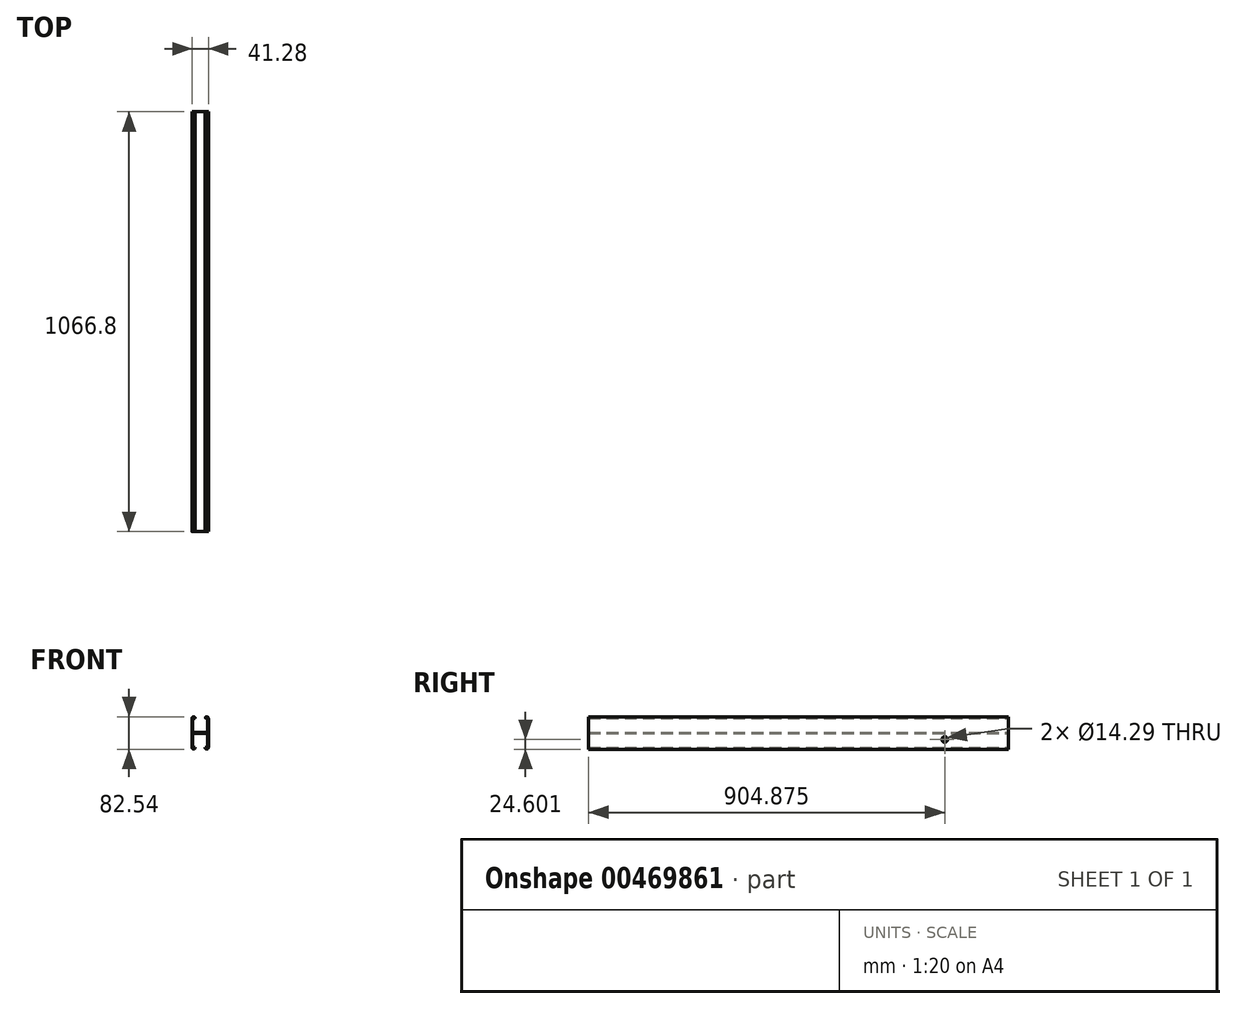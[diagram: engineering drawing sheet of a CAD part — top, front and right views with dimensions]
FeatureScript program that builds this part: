
annotation { "Feature Type Name" : "Feature", "Feature Type Description" : "" }
export const myFeature = defineFeature(function(context is Context, id is Id, definition is map)
    precondition{}
    {
        {
            var Q0;
            Q0=qCreatedBy(makeId("Front.planeOp"),FACE);
            var sketch = newSketch(context, id + "F0", { "sketchPlane" : qUnion([Q0])});
            skLineSegment(sketch, "E0.bottom", {"start": v(0, 0) * mm, "end": v(41.28, 0) * mm});
            skLineSegment(sketch, "E0.left", {"start": v(0, 0) * mm, "end": v(0, 37.3) * mm});
            skLineSegment(sketch, "E0.right", {"start": v(41.28, 0) * mm, "end": v(41.27, 37.3) * mm});
            skLineSegment(sketch, "E1.0", {"start": v(1.59, 1.59) * mm, "end": v(1.59, 37.3) * mm});
            skLineSegment(sketch, "E2.0", {"start": v(1.59, 1.59) * mm, "end": v(39.69, 1.59) * mm});
            skLineSegment(sketch, "E3.0", {"start": v(39.69, 1.59) * mm, "end": v(39.69, 37.3) * mm});
            skArc(sketch, "E4", {"start": v(7.94, 37.3) * mm, "mid": v(3.97, 41.28) * mm, "end": v(0, 37.3) * mm});
            skArc(sketch, "E5", {"start": v(6.35, 37.3) * mm, "mid": v(3.97, 39.69) * mm, "end": v(1.59, 37.3) * mm});
            skArc(sketch, "E6.MirrorC", {"start": v(33.34, 37.3) * mm, "mid": v(37.3, 41.28) * mm, "end": v(41.27, 37.3) * mm});
            skArc(sketch, "E7.MirrorC", {"start": v(34.92, 37.3) * mm, "mid": v(37.3, 39.69) * mm, "end": v(39.69, 37.3) * mm});
            skLineSegment(sketch, "E8.trimOffspring", {"start": v(33.34, 37.3) * mm, "end": v(34.92, 37.3) * mm});
            skLineSegment(sketch, "E9.trimOffspring", {"start": v(20.64, 1.59) * mm, "end": v(20.64, 0) * mm});
            skPoint(sketch, "E10.start.orphan", {"position": v(20.64, 41.28) * mm});
            skPoint(sketch, "E11.orphan", {"position": v(0, 41.28) * mm});
            skLineSegment(sketch, "E12.trimOffspring", {"start": v(6.35, 37.3) * mm, "end": v(7.94, 37.3) * mm});
            skPoint(sketch, "E13.orphan", {"position": v(41.27, 41.28) * mm});
            skLineSegment(sketch, "E14.MirrorCS", {"start": v(6.35, -37.3) * mm, "end": v(7.94, -37.3) * mm});
            skLineSegment(sketch, "E15.MirrorCS", {"start": v(33.34, -37.3) * mm, "end": v(34.92, -37.3) * mm});
            skLineSegment(sketch, "E16.MirrorCS", {"start": v(20.64, -1.59) * mm, "end": v(20.64, 0) * mm});
            skArc(sketch, "E17.MirrorCS", {"start": v(34.92, -37.3) * mm, "mid": v(37.3, -39.69) * mm, "end": v(39.69, -37.3) * mm});
            skArc(sketch, "E18.MirrorCS", {"start": v(33.34, -37.3) * mm, "mid": v(37.3, -41.28) * mm, "end": v(41.27, -37.3) * mm});
            skArc(sketch, "E19.MirrorCS", {"start": v(6.35, -37.3) * mm, "mid": v(3.97, -39.69) * mm, "end": v(1.59, -37.3) * mm});
            skArc(sketch, "E20.MirrorCS", {"start": v(7.94, -37.3) * mm, "mid": v(3.97, -41.28) * mm, "end": v(0, -37.3) * mm});
            skPoint(sketch, "E21.MirrorP", {"position": v(41.27, -41.28) * mm});
            skLineSegment(sketch, "E22.MirrorCS", {"start": v(39.69, -1.59) * mm, "end": v(39.69, -37.3) * mm});
            skLineSegment(sketch, "E23.MirrorCS", {"start": v(1.59, -1.59) * mm, "end": v(39.69, -1.59) * mm});
            skLineSegment(sketch, "E24.MirrorCS", {"start": v(1.59, -1.59) * mm, "end": v(1.59, -37.3) * mm});
            skLineSegment(sketch, "E25.MirrorCS", {"start": v(41.28, 0) * mm, "end": v(41.27, -37.3) * mm});
            skLineSegment(sketch, "E26.MirrorCS", {"start": v(0, 0) * mm, "end": v(0, -37.3) * mm});
            skPoint(sketch, "E27.MirrorP", {"position": v(0, -41.28) * mm});
            skPoint(sketch, "E28.MirrorP", {"position": v(20.64, -41.28) * mm});
            skSolve(sketch);
        }
        {
            var Q0;
            Q0 = qSketchRegion(id + "F0", true);
            extrude(context, id + "F1", {"entities" : qUnion([Q0]), "endBound" : BoundingType.SYMMETRIC, "depth" : 1066.8 * mm});
        }
        {
            var Q0;
            Q0=makeQuery(id+"F1.opExtrude","SWEPT_EDGE",EDGE,{"disambiguationData":[OSD([sQuery(id+"F0.wireOp",EDGE,"E5"),sQuery(id+"F0.wireOp",EDGE,"E12.trimOffspring")])]});
            var Q1;
            Q1=makeQuery(id+"F1.opExtrude","SWEPT_EDGE",EDGE,{"disambiguationData":[OSD([sQuery(id+"F0.wireOp",EDGE,"E4"),sQuery(id+"F0.wireOp",EDGE,"E12.trimOffspring")])]});
            var Q2;
            Q2=makeQuery(id+"F1.opExtrude","SWEPT_EDGE",EDGE,{"disambiguationData":[OSD([sQuery(id+"F0.wireOp",EDGE,"E6.MirrorC"),sQuery(id+"F0.wireOp",EDGE,"E8.trimOffspring")])]});
            var Q3;
            Q3=makeQuery(id+"F1.opExtrude","SWEPT_EDGE",EDGE,{"disambiguationData":[OSD([sQuery(id+"F0.wireOp",EDGE,"E7.MirrorC"),sQuery(id+"F0.wireOp",EDGE,"E8.trimOffspring")])]});
            var Q4;
            Q4=makeQuery(id+"F1.opExtrude","SWEPT_EDGE",EDGE,{"disambiguationData":[OSD([sQuery(id+"F0.wireOp",EDGE,"E0.bottom"),sQuery(id+"F0.wireOp",EDGE,"E0.left")])]});
            var Q5;
            Q5=makeQuery(id+"F1.opExtrude","SWEPT_EDGE",EDGE,{"disambiguationData":[OSD([sQuery(id+"F0.wireOp",EDGE,"E0.bottom"),sQuery(id+"F0.wireOp",EDGE,"E0.right")])]});
            var Q6;
            Q6=makeQuery(id+"F1.opExtrude","SWEPT_EDGE",EDGE,{"disambiguationData":[OSD([sQuery(id+"F0.wireOp",EDGE,"E2.0"),sQuery(id+"F0.wireOp",EDGE,"E3.0")])]});
            var Q7;
            Q7=makeQuery(id+"F1.opExtrude","SWEPT_EDGE",EDGE,{"disambiguationData":[OSD([sQuery(id+"F0.wireOp",EDGE,"E1.0"),sQuery(id+"F0.wireOp",EDGE,"E2.0")])]});
            fillet(context, id + "F2", {"entities" : qUnion([Q0, Q1, Q2, Q3, Q4, Q5, Q6, Q7]), "radius" : 0.8 * mm, "tangentPropagation" : true, "allowEdgeOverflow" : false});
        }
        {
            var Q0;
            Q0=makeQuery(id+"F1.opExtrude","SWEPT_FACE",FACE,{"disambiguationData":[OSD([sQuery(id+"F0.wireOp",EDGE,"E0.right"),sQuery(id+"F0.wireOp",EDGE,"E25.MirrorCS")])]});
            var sketch = newSketch(context, id + "F3", { "sketchPlane" : qUnion([Q0])});
            skCircle(sketch, "E29", {"center": v(371.48, -16.67) * mm, "radius": 7.14 * mm});
            skSolve(sketch);
        }
        {
            var Q0;
            Q0 = qSketchRegion(id + "F3", true);
            extrude(context, id + "F4", {"entities" : qUnion([Q0]), "operationType" : NewBodyOperationType.REMOVE, "endBound" : BoundingType.THROUGH_ALL, "oppositeDirection" : true, "depth" : 25.4 * mm});
        }
    });
